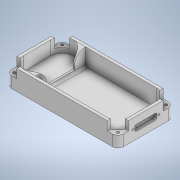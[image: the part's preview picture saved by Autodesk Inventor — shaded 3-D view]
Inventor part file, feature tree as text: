
AUTODESK INVENTOR PART (.ipt)
format: ipt  version: 2020.3 (Build 243373000, 373)  size: 421,376 bytes
history: native  units: mm
features: extrude x9, sketch x8, fillet x6, hole x1
ambient origin geometry x8: Origin, YZ Plane, XZ Plane, XY Plane, X Axis, Y Axis, Z Axis, Center Point
bodies: Solid1 (feature_tree)
feature tree (24):
  extrude  "Extrusion1"  Depth=100.0mm
  extrude  "Extrusion2"  Depth=5.0mm
  fillet  "Fillet1"  Radius=5.0mm
  fillet  "Fillet2"  Radius=5.0mm
  hole  "Hole1"  [1 undecoded]
  extrude  "Extrusion7"  Depth=20.0mm
  fillet  "Fillet6"  Radius=200.0mm
  sketch  "Sketch12"  dims[d10=10.0mm d11=20.0mm d12=200.0mm]
  extrude  "Extrusion9"  Depth=100.0mm
  extrude  "Extrusion10"  Depth=7.0mm
  fillet  "Fillet7"  Radius=7.0mm
  fillet  "Fillet8"  Radius=36.0mm
  extrude  "Extrusion13"  Depth=5.0mm
  extrude  "Extrusion14"  Depth=5.0mm
  fillet  "Fillet11"  Radius=13.5mm
  extrude  "Extrusion15"  Depth=5.0mm
  extrude  "Extrusion16"  Depth=3.0mm
  sketch  "Sketch2"  dims[d0=200.0mm d1=100.0mm]
  sketch  "Sketch3"  dims[d2=11.0mm d3=0.0mm d4=5.0mm d5=5.0mm d6=5.0mm]
  sketch  "Sketch4"  dims[d7=5.0mm d8=25.0mm d9=0.0mm]
  sketch  "Sketch13"  dims[d13=100.0mm d14=7.0mm]
  sketch  "Sketch15"  dims[d15=7.0mm d16=7.0mm d17=7.0mm]
  sketch  "Sketch17"  dims[d18=5.0mm d19=6.0mm d20=4.0mm d21=2.0mm d22=90.0deg d23=18.0mm d24=0.0mm d31=36.0mm]
  sketch  "Sketch18"  dims[d32=80.0mm d33=13.5mm d34=11.75mm d35=13.5mm d36=11.75mm d37=3.0mm d38=3.0mm d39=3.0mm d40=6.25mm d41=3.0mm d42=6.25mm d43=3.0mm d44=3.0mm d45=6.0mm d46=1.0mm d47=6.0mm d48=1.0mm d49=1.5mm d50=1.5mm d51=1.5mm d52=1.5mm d56=50.0mm d57=38.45mm d58=25.0mm d59=7.5mm d60=3.75mm d61=1.0mm d63=180.0deg d64=12.0mm d115=2.0mm d116=2.0mm d119=25.0mm d120=0.0mm d121=20.0mm d122=4.0mm d123=186.0mm d124=86.0mm d125=186.0mm d126=86.0mm d129=16.0mm d130=0.0mm d131=10.0mm d132=25.0mm d133=200.0mm d134=100.0mm d135=100.0mm d136=100.0mm d137=6.0mm d138=0.0mm d139=2.0mm d140=4.0mm d141=2.35mm d142=2.35mm d143=60.0deg d144=1.0mm d145=1.0mm d148=0.5mm d149=0.5mm d150=0.5mm d151=0.5mm d155=10.0mm d156=0.0mm d159=2.75mm d161=4.0mm d162=0.0mm d164=2.7mm d165=6.0mm d166=0.0mm d167=8.5mm d168=8.5mm d169=5.0mm d170=0.0mm d53=0.5mm d54=0.872665mm d55=0.5mm]
note: 1 required parameter value undecoded (feature->parameter linkage not recoverable at this tier; creation-order binding heuristic only, values carry confidence <= 0.55)
